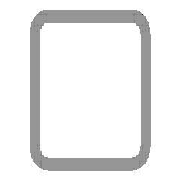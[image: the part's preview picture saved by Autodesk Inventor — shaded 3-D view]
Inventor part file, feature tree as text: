
AUTODESK INVENTOR PART (.ipt)
format: ipt  version: 2025.1 (Build 291241020, 241B)  size: 145,408 bytes
history: native  units: mm (DEFAULTED — no unit token found)
features: other x4, sketch x1, plane x1
ambient origin geometry x8: Origin, YZ Plane, XZ Plane, XY Plane, X Axis, Y Axis, Z Axis, Center Point
bodies: Solid1 (feature_tree), Body (feature_tree)
feature tree (6):
  parser-record x1  (decoder bookkeeping rows leaked as tree rows — omitted from the tree; the rows remain in map.json)
  other  "Driven Length"
  other  "Start plane"
  other  "End plane"
  sketch  "Sketch3"  dims[d3=1350.0mm d4=0.0mm d7=6.0mm d9=100.0mm d11=100.0mm d12=3.0mm d13=50.0mm d14=1400.0mm d15=50.0mm d16=50.0mm d17=90.0deg d18=1350.0mm]
  plane  "Work Plane3"
